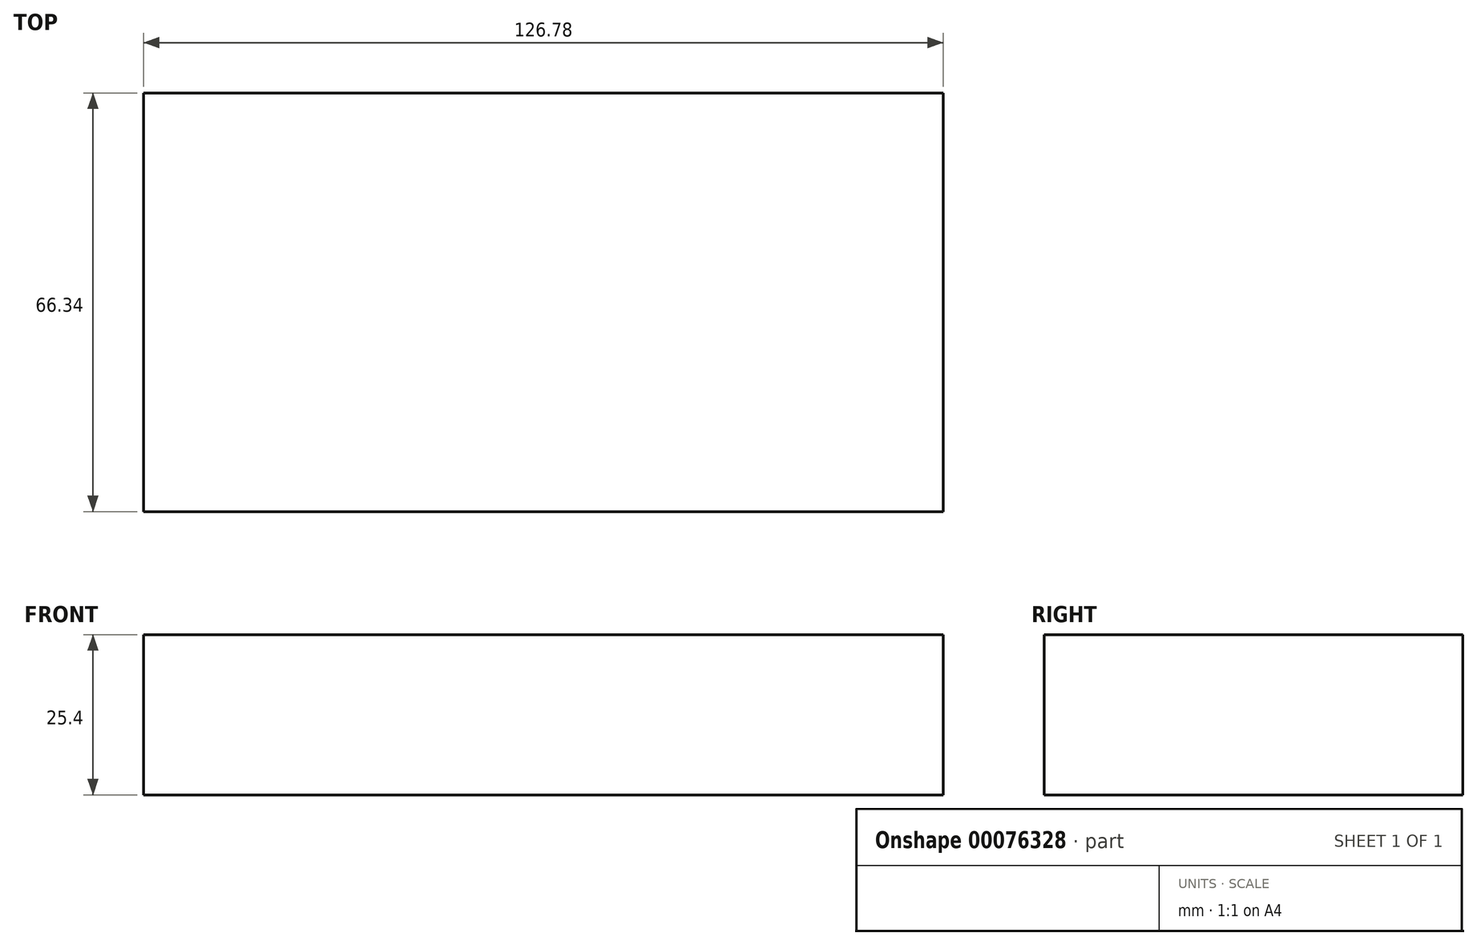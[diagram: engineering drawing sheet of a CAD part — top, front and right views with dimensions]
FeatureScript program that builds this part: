
annotation { "Feature Type Name" : "Feature", "Feature Type Description" : "" }
export const myFeature = defineFeature(function(context is Context, id is Id, definition is map)
    precondition{}
    {
        {
            var Q0;
            Q0=qCreatedBy(makeId("Top.planeOp"),FACE);
            var sketch = newSketch(context, id + "F0", { "sketchPlane" : qUnion([Q0])});
            skLineSegment(sketch, "E0.bottom", {"start": v(-61.46, 66.34) * mm, "end": v(65.32, 66.34) * mm});
            skLineSegment(sketch, "E0.top", {"start": v(-61.46, 0) * mm, "end": v(65.32, 0) * mm});
            skLineSegment(sketch, "E0.left", {"start": v(-61.46, 66.34) * mm, "end": v(-61.46, 0) * mm});
            skLineSegment(sketch, "E0.right", {"start": v(65.32, 66.34) * mm, "end": v(65.32, 0) * mm});
            skSolve(sketch);
        }
        {
            var Q0;
            Q0=makeQuery(id+"F0.imprint","IMPRINT",FACE,{"disambiguationData":[TD([[makeQuery(id+"F0.imprint","IMPRINT",EDGE,{"derivedFrom":sQuery(id+"F0.wireOp",EDGE,"E0.bottom")}),-1.0]])]});
            extrude(context, id + "F1", {"entities" : qUnion([Q0]), "depth" : 25.4 * mm});
        }
        {
            var Q0;
            Q0=makeQuery(id+"F1.opExtrude","CAP_FACE",FACE,{"disambiguationData":[OSD([sQuery(id+"F0.wireOp",EDGE,"E0.bottom"),sQuery(id+"F0.wireOp",EDGE,"E0.top"),sQuery(id+"F0.wireOp",EDGE,"E0.left"),sQuery(id+"F0.wireOp",EDGE,"E0.right")])],"isStart":false});
            extrude(context, id + "F2", {"entities" : qUnion([Q0]), "operationType" : NewBodyOperationType.REMOVE, "endBound" : BoundingType.THROUGH_ALL, "depth" : 25.4 * mm});
        }
    });
